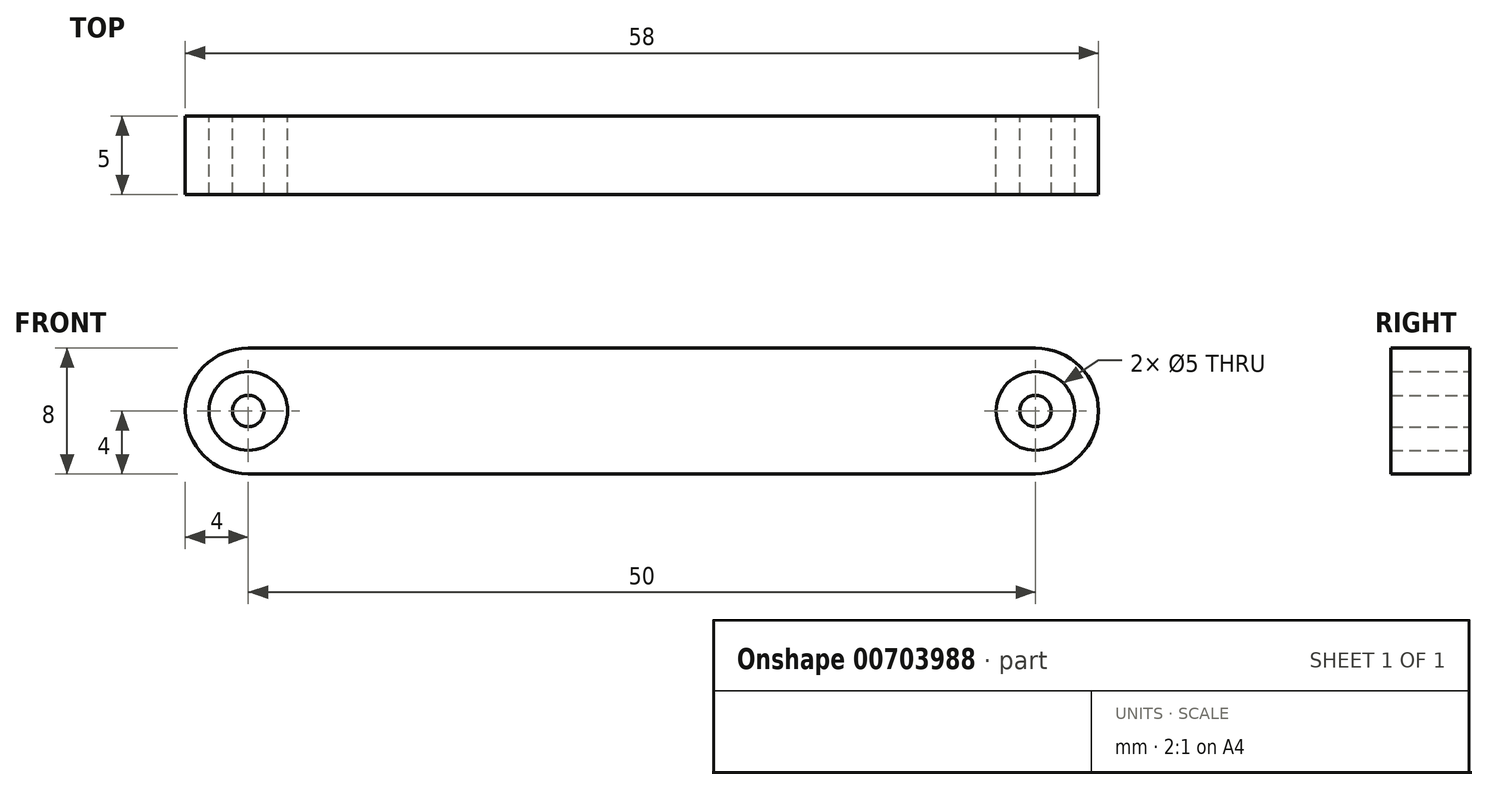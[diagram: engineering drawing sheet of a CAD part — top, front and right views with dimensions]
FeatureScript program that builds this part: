
annotation { "Feature Type Name" : "Feature", "Feature Type Description" : "" }
export const myFeature = defineFeature(function(context is Context, id is Id, definition is map)
    precondition{}
    {
        {
            var Q0;
            Q0=qCreatedBy(makeId("Front.planeOp"),FACE);
            var sketch = newSketch(context, id + "F0", { "sketchPlane" : qUnion([Q0])});
            skLineSegment(sketch, "E0.bottom", {"start": v(0, 0) * mm, "end": v(50, 0) * mm});
            skLineSegment(sketch, "E0.top", {"start": v(0, 8) * mm, "end": v(50, 8) * mm});
            skArc(sketch, "E1", {"start": v(50, 0) * mm, "mid": v(54, 4) * mm, "end": v(50, 8) * mm});
            skArc(sketch, "E2", {"start": v(0, 8) * mm, "mid": v(-4, 4) * mm, "end": v(0, 0) * mm});
            skCircle(sketch, "E3", {"center": v(0, 4) * mm, "radius": 2.5 * mm});
            skCircle(sketch, "E4", {"center": v(0, 4) * mm, "radius": 1 * mm});
            skCircle(sketch, "E5", {"center": v(50, 4) * mm, "radius": 2.5 * mm});
            skCircle(sketch, "E6", {"center": v(50, 4) * mm, "radius": 1 * mm});
            skSolve(sketch);
        }
        {
            var Q0;
            Q0 = qSketchRegion(id + "F0", true);
            var Q1;
            Q1=makeQuery(id+"F0.imprint","IMPRINT",FACE,{"disambiguationData":[TD([[makeQuery(id+"F0.imprint","IMPRINT",EDGE,{"derivedFrom":sQuery(id+"F0.wireOp",EDGE,"E4")}),1.0]])]});
            var Q2;
            Q2=makeQuery(id+"F0.imprint","IMPRINT",FACE,{"disambiguationData":[TD([[makeQuery(id+"F0.imprint","IMPRINT",EDGE,{"derivedFrom":sQuery(id+"F0.wireOp",EDGE,"E6")}),1.0]])]});
            extrude(context, id + "F1", {"entities" : qUnion([Q0, Q1, Q2]), "depth" : 5 * mm, "offsetDistance" : 25 * mm});
        }
    });
